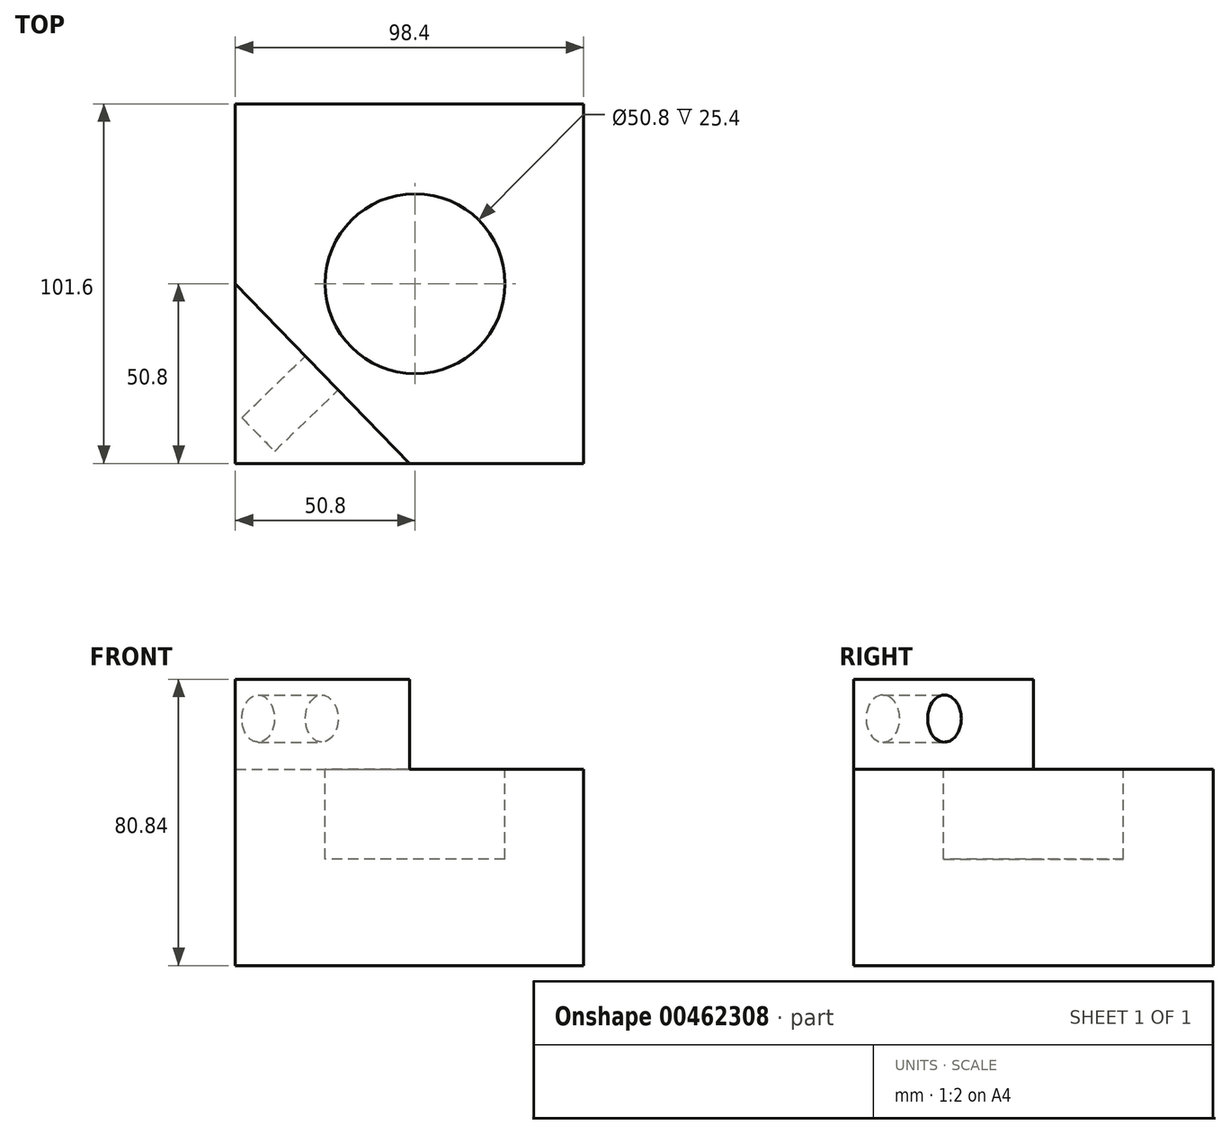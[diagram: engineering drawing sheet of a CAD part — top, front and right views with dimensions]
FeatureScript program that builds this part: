
annotation { "Feature Type Name" : "Feature", "Feature Type Description" : "" }
export const myFeature = defineFeature(function(context is Context, id is Id, definition is map)
    precondition{}
    {
        {
            var Q0;
            Q0=qCreatedBy(makeId("Front.planeOp"),FACE);
            var sketch = newSketch(context, id + "F0", { "sketchPlane" : qUnion([Q0])});
            skLineSegment(sketch, "E0", {"start": v(0, 0) * mm, "end": v(0, 55.44) * mm});
            skLineSegment(sketch, "E1", {"start": v(0, 55.44) * mm, "end": v(98.4, 55.44) * mm});
            skLineSegment(sketch, "E2", {"start": v(98.4, 55.44) * mm, "end": v(98.4, 0) * mm});
            skLineSegment(sketch, "E3", {"start": v(98.4, 0) * mm, "end": v(0, 0) * mm});
            skSolve(sketch);
        }
        {
            var Q0;
            Q0=makeQuery(id+"F0.imprint","IMPRINT",FACE,{"disambiguationData":[TD([[makeQuery(id+"F0.imprint","IMPRINT",EDGE,{"derivedFrom":sQuery(id+"F0.wireOp",EDGE,"E0")}),-1.0]])]});
            extrude(context, id + "F1", {"entities" : qUnion([Q0]), "depth" : 101.6 * mm});
        }
        {
            var Q0;
            Q0=makeQuery(id+"F1.opExtrude","SWEPT_FACE",FACE,{"disambiguationData":[OSD([sQuery(id+"F0.wireOp",EDGE,"E1")])]});
            var sketch = newSketch(context, id + "F2", { "sketchPlane" : qUnion([Q0])});
            skCircle(sketch, "E4", {"center": v(50.8, -50.8) * mm, "radius": 25.4 * mm});
            skSolve(sketch);
        }
        {
            var Q0;
            Q0=makeQuery(id+"F2.imprint","IMPRINT",FACE,{"disambiguationData":[TD([[makeQuery(id+"F2.imprint","IMPRINT",EDGE,{"derivedFrom":sQuery(id+"F2.wireOp",EDGE,"E4")}),1.0]])]});
            extrude(context, id + "F3", {"entities" : qUnion([Q0]), "operationType" : NewBodyOperationType.REMOVE, "oppositeDirection" : true, "depth" : 25.4 * mm});
        }
        {
            var Q0;
            Q0=makeQuery(id+"F1.opExtrude","SWEPT_FACE",FACE,{"disambiguationData":[OSD([sQuery(id+"F0.wireOp",EDGE,"E1")])]});
            var sketch = newSketch(context, id + "F4", { "sketchPlane" : qUnion([Q0])});
            skLineSegment(sketch, "E5", {"start": v(0, -50.8) * mm, "end": v(49.2, -101.6) * mm});
            skLineSegment(sketch, "E6", {"start": v(49.2, -101.6) * mm, "end": v(0, -101.6) * mm});
            skLineSegment(sketch, "E7", {"start": v(0, -101.6) * mm, "end": v(0, -50.8) * mm});
            skSolve(sketch);
        }
        {
            var Q0;
            Q0=makeQuery(id+"F4.imprint","IMPRINT",FACE,{"disambiguationData":[TD([[makeQuery(id+"F4.imprint","IMPRINT",EDGE,{"derivedFrom":sQuery(id+"F4.wireOp",EDGE,"E5")}),-1.0]])]});
            var Q1;
            Q1=sQuery(id+"F4.wireOp",EDGE,"E5");
            var Q2;
            Q2=sQuery(id+"F4.wireOp",EDGE,"E6");
            var Q3;
            Q3=sQuery(id+"F4.wireOp",EDGE,"E7");
            extrude(context, id + "F5", {"entities" : qUnion([Q0]), "operationType" : NewBodyOperationType.ADD, "surfaceEntities" : qUnion([Q1, Q2, Q3]), "depth" : 25.4 * mm});
        }
        {
            var Q0;
            Q0=makeQuery(id+"F5.opExtrude","SWEPT_FACE",FACE,{"disambiguationData":[OSD([sQuery(id+"F4.wireOp",EDGE,"E5")])]});
            var sketch = newSketch(context, id + "F6", { "sketchPlane" : qUnion([Q0])});
            skCircle(sketch, "E8", {"center": v(-71.58, 69.76) * mm, "radius": 6.64 * mm});
            skSolve(sketch);
        }
        {
            var Q0;
            Q0=makeQuery(id+"F6.imprint","IMPRINT",FACE,{"disambiguationData":[TD([[makeQuery(id+"F6.imprint","IMPRINT",EDGE,{"derivedFrom":sQuery(id+"F6.wireOp",EDGE,"E8")}),1.0]])]});
            var Q1;
            Q1=sQuery(id+"F6.wireOp",EDGE,"E8");
            extrude(context, id + "F7", {"entities" : qUnion([Q0]), "operationType" : NewBodyOperationType.REMOVE, "surfaceEntities" : qUnion([Q1]), "oppositeDirection" : true, "depth" : 25 * mm});
        }
    });
